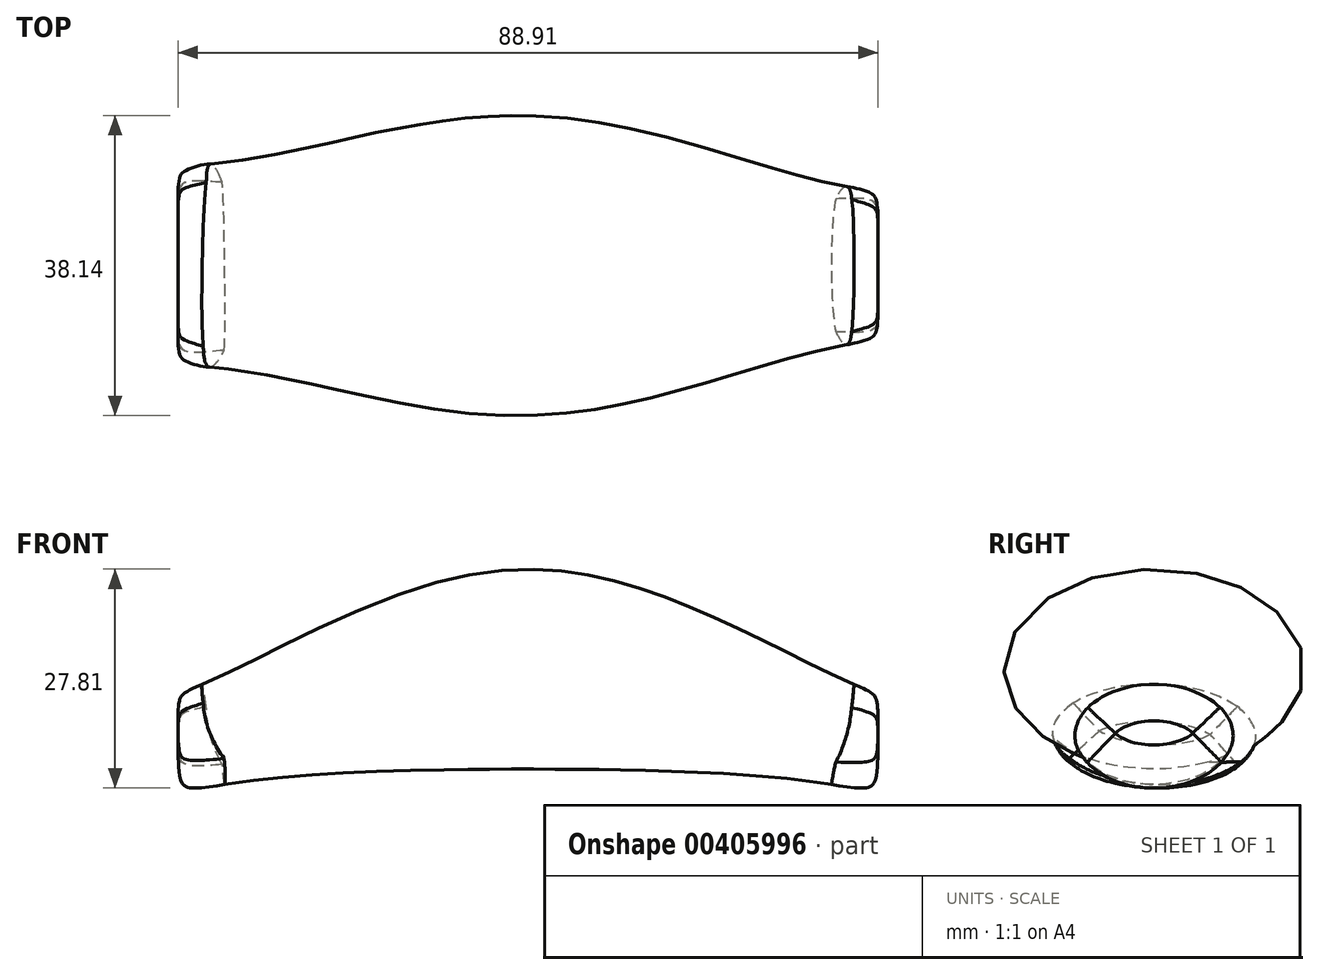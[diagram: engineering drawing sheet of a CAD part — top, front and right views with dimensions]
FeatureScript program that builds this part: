
annotation { "Feature Type Name" : "Feature", "Feature Type Description" : "" }
export const myFeature = defineFeature(function(context is Context, id is Id, definition is map)
    precondition{}
    {
        {
            var Q0;
            Q0=qCreatedBy(makeId("Right.planeOp"),FACE);
            var sketch = newSketch(context, id + "F0", { "sketchPlane" : qUnion([Q0])});
            skEllipse(sketch, "E0", {"center": v(0, 0) * mm, "majorRadius": 19.05 * mm, "minorRadius": 12.7 * mm, "majorAxis": v(1, 0)});
            skSolve(sketch);
        }
        {
            var Q0;
            Q0=qCreatedBy(makeId("Right.planeOp"),FACE);
            cPlane(context, id + "F1", {"entities" : qUnion([Q0]), "cplaneType" : CPlaneType.OFFSET, "offset" : 44.45 * mm, "width" : 152.4 * mm, "height" : 152.4 * mm});
        }
        {
            var Q0;
            Q0=qCreatedBy(id+"F1.planeOp",FACE);
            var sketch = newSketch(context, id + "F2", { "sketchPlane" : qUnion([Q0])});
            skEllipse(sketch, "E1", {"center": v(0, -9.53) * mm, "majorRadius": 9.53 * mm, "minorRadius": 6.35 * mm, "majorAxis": v(1, 0)});
            skSolve(sketch);
        }
        {
            var Q0;
            Q0=qCreatedBy(makeId("Right.planeOp"),FACE);
            cPlane(context, id + "F3", {"entities" : qUnion([Q0]), "cplaneType" : CPlaneType.OFFSET, "offset" : 44.45 * mm, "oppositeDirection" : true, "width" : 152.4 * mm, "height" : 152.4 * mm});
        }
        {
            var Q0;
            Q0=qCreatedBy(id+"F3.planeOp",FACE);
            var sketch = newSketch(context, id + "F4", { "sketchPlane" : qUnion([Q0])});
            skEllipse(sketch, "E2.0", {"center": v(0, -9.53) * mm, "majorRadius": 12.7 * mm, "minorRadius": 6.35 * mm, "majorAxis": v(1, 0)});
            skSolve(sketch);
        }
        {
            var Q0;
            Q0=qCreatedBy(makeId("Front.planeOp"),FACE);
            var sketch = newSketch(context, id + "F5", { "sketchPlane" : qUnion([Q0])});
            skArc(sketch, "E3", {"start": v(44.45, -9.52) * mm, "mid": v(0, 0) * mm, "end": v(-44.45, -9.52) * mm});
            skSolve(sketch);
        }
        {
            var Q0;
            Q0=makeQuery(id+"F4.imprint","IMPRINT",FACE,{"disambiguationData":[TD([[makeQuery(id+"F4.imprint","IMPRINT",EDGE,{"derivedFrom":sQuery(id+"F4.wireOp",EDGE,"E2.0")}),1.0]])]});
            var Q1;
            Q1=makeQuery(id+"F0.imprint","IMPRINT",FACE,{"disambiguationData":[TD([[makeQuery(id+"F0.imprint","IMPRINT",EDGE,{"derivedFrom":sQuery(id+"F0.wireOp",EDGE,"E0")}),1.0]])]});
            var Q2;
            Q2=makeQuery(id+"F2.imprint","IMPRINT",FACE,{"disambiguationData":[TD([[makeQuery(id+"F2.imprint","IMPRINT",EDGE,{"derivedFrom":sQuery(id+"F2.wireOp",EDGE,"E1")}),1.0]])]});
            var Q3;
            Q3=sQuery(id+"F5.wireOp",EDGE,"E3");
            loft(context, id + "F6", {"sheetProfilesArray" : [{ "sheetProfileEntities" : qUnion([Q0]) }, { "sheetProfileEntities" : qUnion([Q1]) }, { "sheetProfileEntities" : qUnion([Q2]) }], "guidesArray" : [{ "guideEntities" : qUnion([Q3]), "guideDerivativeType" : LoftGuideDerivativeType.DEFAULT, "guideDerivativeMagnitude" : 1 }]});
        }
        {
            var Q0;
            Q0=makeQuery(id+"F6.opLoft","MID_CAP_EDGE",EDGE,{"disambiguationData":[OSD([sQuery(id+"F4.wireOp",EDGE,"E2.0")])],"capPos":0.0});
            var Q1;
            Q1=makeQuery(id+"F6.opLoft","MID_CAP_EDGE",EDGE,{"disambiguationData":[OSD([sQuery(id+"F2.wireOp",EDGE,"E1"),sQuery(id+"F4.wireOp",EDGE,"E2.0")])],"capPos":2.0});
            fillet(context, id + "F7", {"entities" : qUnion([Q0, Q1]), "radius" : 5.08 * mm, "tangentPropagation" : true, "rho" : .75, "crossSection" : FilletCrossSection.CONIC, "allowEdgeOverflow" : false});
        }
    });
